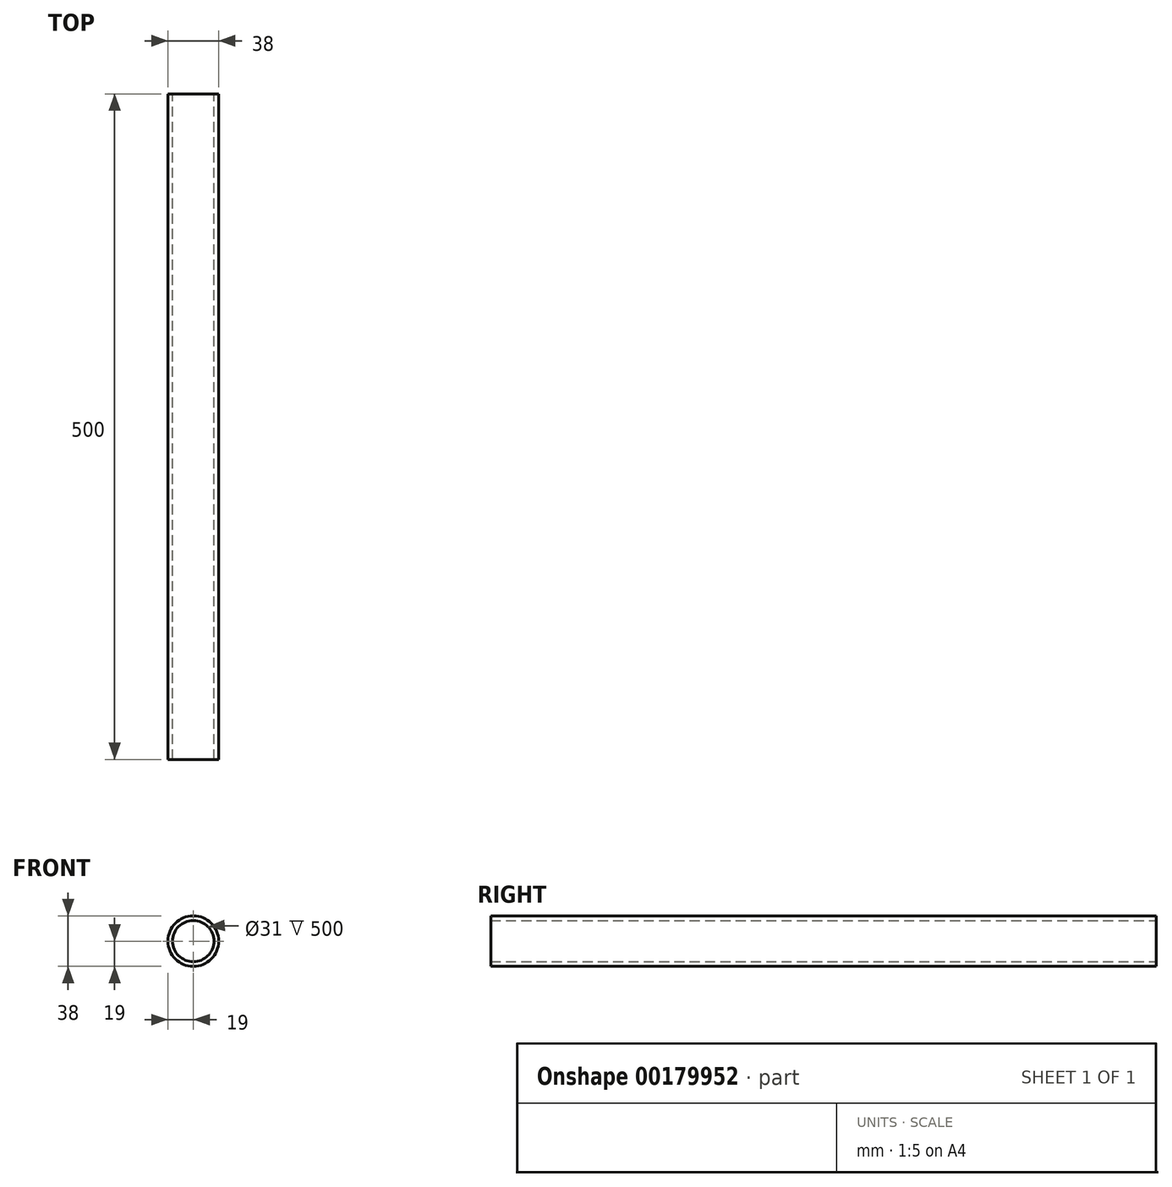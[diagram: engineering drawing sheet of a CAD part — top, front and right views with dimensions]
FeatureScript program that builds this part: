
annotation { "Feature Type Name" : "Feature", "Feature Type Description" : "" }
export const myFeature = defineFeature(function(context is Context, id is Id, definition is map)
    precondition{}
    {
        {
            var Q0;
            Q0=qCreatedBy(makeId("Front.planeOp"),FACE);
            var sketch = newSketch(context, id + "F0", { "sketchPlane" : qUnion([Q0])});
            skCircle(sketch, "E0", {"center": v(0, 0) * mm, "radius": 19 * mm});
            skCircle(sketch, "E1.0", {"center": v(0, 0) * mm, "radius": 15.5 * mm});
            skSolve(sketch);
        }
        {
            var Q0;
            Q0=qCreatedBy(makeId("Right.planeOp"),FACE);
            var sketch = newSketch(context, id + "F1", { "sketchPlane" : qUnion([Q0])});
            skLineSegment(sketch, "E2", {"start": v(0, 0) * mm, "end": v(500, 0) * mm});
            skSolve(sketch);
        }
        {
            var Q0;
            Q0=makeQuery(id+"F0.imprint","IMPRINT",FACE,{"disambiguationData":[TD([[makeQuery(id+"F0.imprint","IMPRINT",EDGE,{"derivedFrom":sQuery(id+"F0.wireOp",EDGE,"E0")}),1.0]])]});
            var Q1;
            Q1=sQuery(id+"F1.wireOp",EDGE,"cREBVvGn-Rh94-WNf2-bF0z-zHwWe6ERPXPu");
            var Q2;
            Q2=sQuery(id+"F1.wireOp",EDGE,"E2");
            var Q3;
            Q3=sQuery(id+"F1.wireOp",EDGE,"PvgMx3XH-LjPc-BSvU-EPw0-JMFL71ncoCQT");
            sweep(context, id + "F2", {"profiles" : qUnion([Q0]), "path" : qUnion([Q1, Q2, Q3])});
        }
    });
